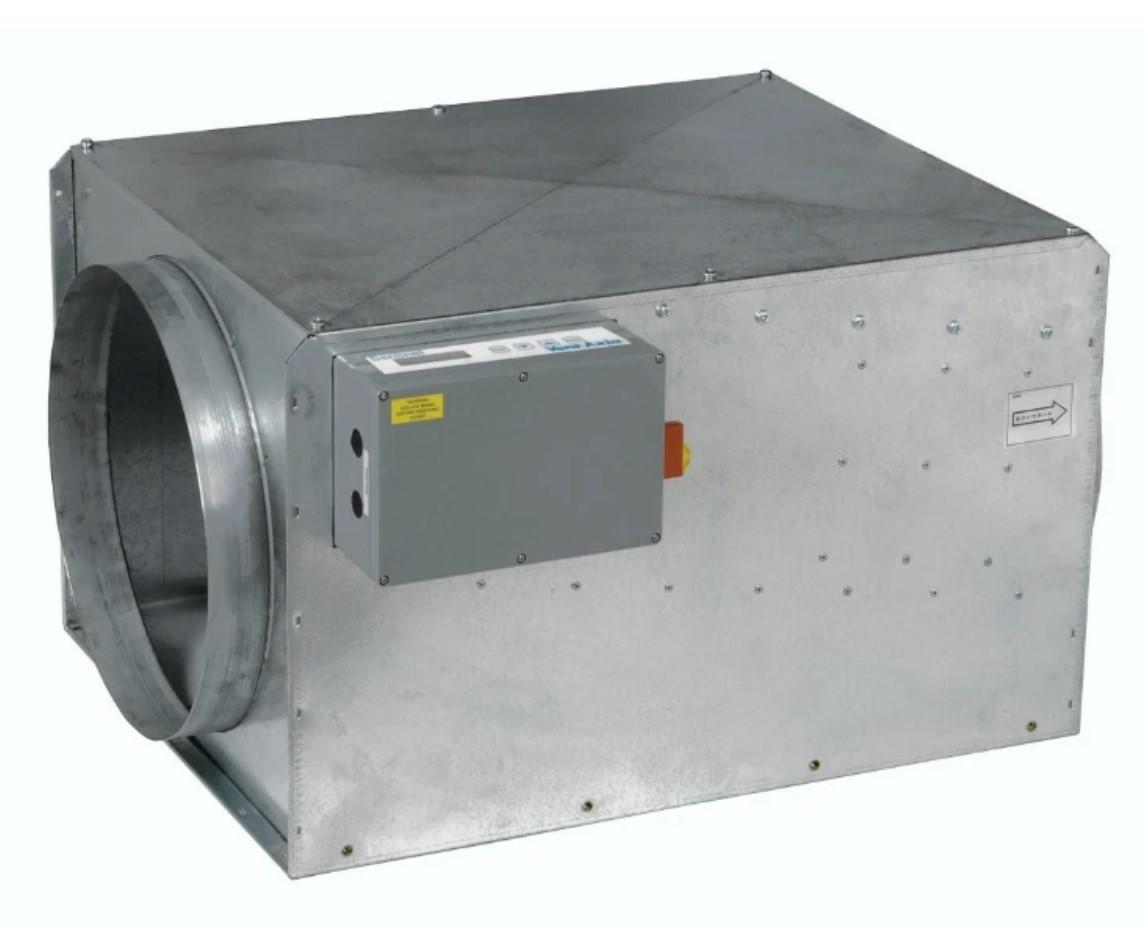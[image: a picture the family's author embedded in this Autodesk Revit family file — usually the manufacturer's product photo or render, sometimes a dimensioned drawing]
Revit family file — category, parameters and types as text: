
# Revit family: CADS_Vent-Axia_MechEquip_Fan_SENT_DBoxSingle - EXTRACT
name_source: partatom
category: Mechanical Equipment
units: mm (PartAtom-declared; Revit-internal decimal feet)

## family parameters
Classification = None
Cut with Voids When Loaded = No
Host = Face
OmniClass Number = 23.75.35.17.11
OmniClass Title = Fans for Air Ductwork
Part Type = Normal
Room Calculation Point = No
Round Connector Dimension = Use Diameter
Shared = No

## types (11) — shared parameters
AirflowRateRange = 0.0 L/s
AssemblyPlace = UNKNOWN
AssetType = FIXED
Default Elevation = 1219 mm
DurationUnit = Year
ExteriorInsulation = No
Fitting Type = Ignore
GrossWeight = 0.00 kg
HasProtectiveEarth = No
IsExtendedWarranty = No
ManufacturerAddress = Fleming Way
Crawley 
RH10 9YX
Quantity = 1
RatedCurrent = 0 A
RatedVoltage = 0 V
Status = New
WarrantyGuarantor = Vent-Axia Limited
WorkingPressure = 0.0 Pa
zero-valued in all types: CADS_Index, CADS_Usage, ExpectedServiceLife, H, NumberOfPoles, W

## per-type parameters (varying)
| type | EBHoffset | EBVoffset | L | ModelReference | NominalDiameter | NominalHeight | NominalLength | NominalWidth | OutOffset | SpigotCLHeight | Type Image |
| SENT100S | 75 mm | 70 mm | 360 mm | SENTINEL 100S/H | 100 mm  [stored 0.328084 ft] | 192 mm  [stored 0.629921 ft] | 380 mm | 306 mm  [stored 1.00394 ft] | 62 mm  [stored 0.203412 ft] | 62 mm  [stored 0.203412 ft] | <None> |
| SENT125S | 206 mm | 80 mm | 360 mm | SENTINEL 125 HIERARCHY | 125 mm  [stored 0.410105 ft] | 192 mm  [stored 0.629921 ft] | 380 mm | 306 mm  [stored 1.00394 ft] | 62 mm  [stored 0.203412 ft] | 62 mm  [stored 0.203412 ft] | <None> |
| SENT150S | 206 mm | 80 mm | 360 mm | SENTINEL 150 HIERARCHY | 150 mm | 192 mm  [stored 0.629921 ft] | 380 mm | 306 mm  [stored 1.00394 ft] | 62 mm  [stored 0.203412 ft] | 62 mm  [stored 0.203412 ft] | <None> |
| SENT150S/CP | 206 mm | 80 mm | 360 mm | SENTINEL 150 CONST.PRESS | 150 mm | 192 mm  [stored 0.629921 ft] | 380 mm | 306 mm  [stored 1.00394 ft] | 62 mm  [stored 0.203412 ft] | 62 mm  [stored 0.203412 ft] | <None> |
| SENT200S | 206 mm | 80 mm | 415 mm | SENTINEL 200 HIERARCHY | 200 mm  [stored 0.656168 ft] | 287 mm | 435 mm | 360 mm | 60 mm | 60 mm | <None> |
| SENT250S | 206 mm | 80 mm | 415 mm | SENTINEL 250 HIERARCHY | 250 mm  [stored 0.82021 ft] | 287 mm | 435 mm | 360 mm | 35 mm | 35 mm | <None> |
| SENT315S | 206 mm | 80 mm | 690 mm | SENTINEL 315 HIERARCHY | 315 mm | 458 mm | 710 mm | 568 mm | 43 mm | 43 mm | <None> |
| SENT315S/CP | 206 mm | 80 mm | 690 mm | SENTINEL 315 CONST.PRESS | 315 mm | 458 mm | 710 mm | 568 mm | 43 mm | 43 mm | <None> |
| SENT400S | 206 mm | 80 mm | 690 mm | SENTINEL 400 HIERARCHY | 400 mm | 458 mm | 710 mm | 568 mm | 43 mm | 43 mm | <None> |
| SENT400S/CP | 206 mm | 80 mm | 690 mm | SENTINEL 400 CONST.PRESS | 400 mm | 458 mm | 710 mm | 568 mm | 43 mm | 43 mm | <None> |
| SENT500S | 206 mm | 80 mm | 878 mm | SENTINEL 500 HIERARCHY | 500 mm | 577 mm | 898 mm | 765 mm | 59 mm | 59 mm | CADS_Vent-Axia_MechEquip_Fan_SENT_DBoxSingle.jpg |

note: column(s) folded — value = type name in every type: ModelNumber

note: [stored X ft] marks values corroborated as IEEE doubles in the binary element streams (Revit-internal decimal feet)

## geometry (parser evidence)
native form markers: Sweep x3
no freeform markers — native parametric forms only
